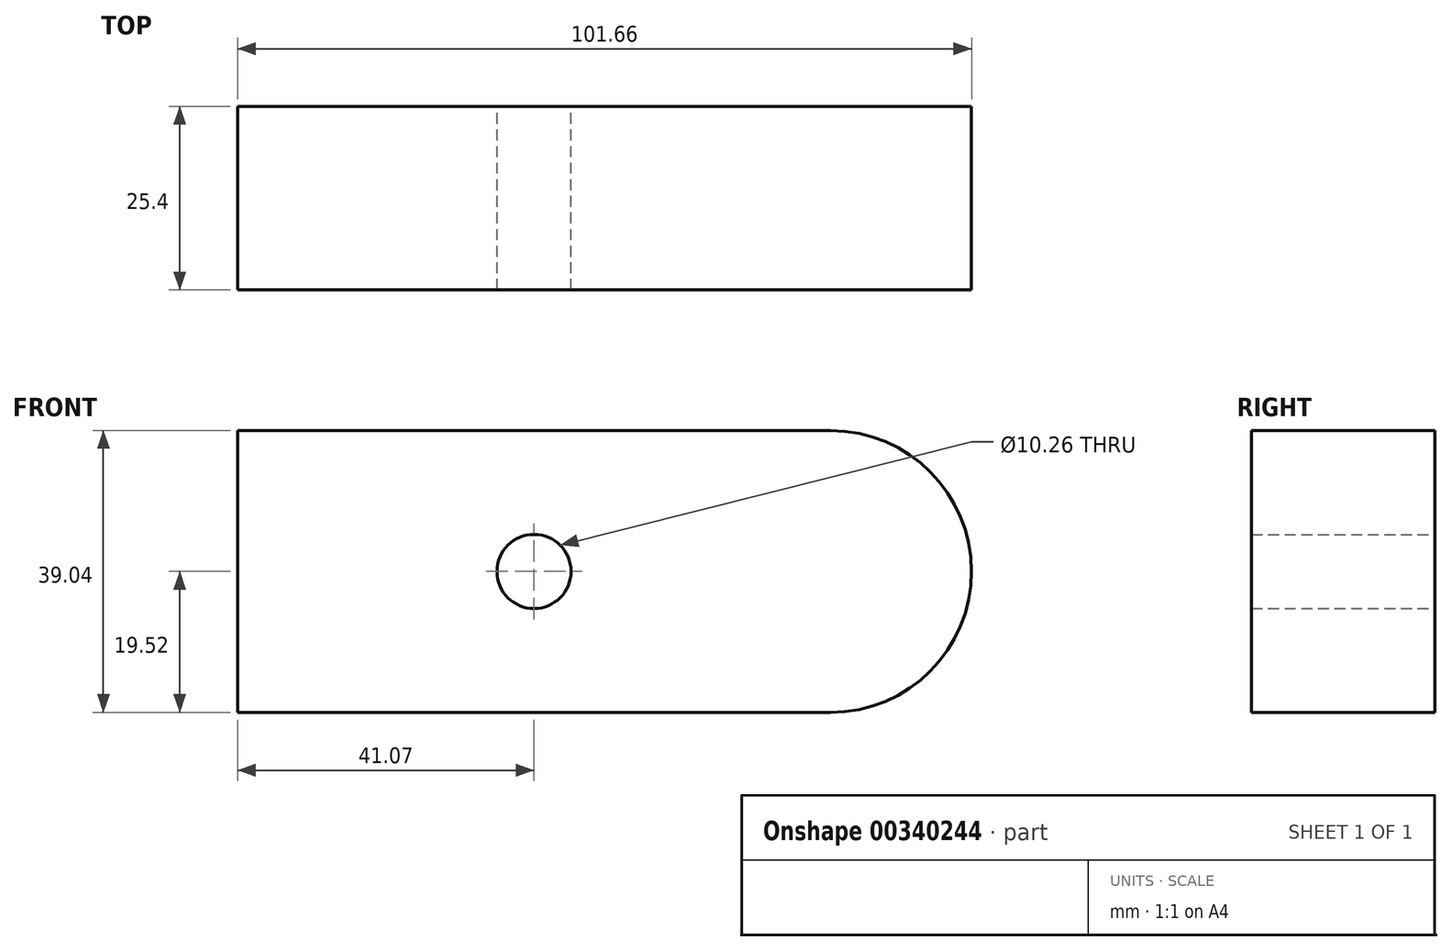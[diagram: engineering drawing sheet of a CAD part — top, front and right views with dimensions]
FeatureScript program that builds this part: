
annotation { "Feature Type Name" : "Feature", "Feature Type Description" : "" }
export const myFeature = defineFeature(function(context is Context, id is Id, definition is map)
    precondition{}
    {
        {
            var Q0;
            Q0=qCreatedBy(makeId("Front.planeOp"),FACE);
            var sketch = newSketch(context, id + "F0", { "sketchPlane" : qUnion([Q0])});
            skLineSegment(sketch, "E0.bottom", {"start": v(41.07, 19.52) * mm, "end": v(-41.07, 19.52) * mm});
            skLineSegment(sketch, "E0.top", {"start": v(41.07, -19.52) * mm, "end": v(-41.07, -19.52) * mm});
            skLineSegment(sketch, "E0.left", {"start": v(41.07, 19.52) * mm, "end": v(41.07, -19.52) * mm});
            skLineSegment(sketch, "E0.right", {"start": v(-41.07, 19.52) * mm, "end": v(-41.07, -19.52) * mm});
            skPoint(sketch, "E0.middle", {"position": v(0, 0) * mm});
            skCircle(sketch, "E1", {"center": v(41.07, 0) * mm, "radius": 19.52 * mm});
            skCircle(sketch, "E2", {"center": v(0, 0) * mm, "radius": 5.13 * mm});
            skSolve(sketch);
        }
        {
            var Q0;
            Q0 = qSketchRegion(id + "F0", true);
            extrude(context, id + "F1", {"entities" : qUnion([Q0]), "depth" : 25.4 * mm});
        }
    });
